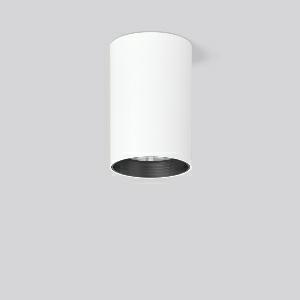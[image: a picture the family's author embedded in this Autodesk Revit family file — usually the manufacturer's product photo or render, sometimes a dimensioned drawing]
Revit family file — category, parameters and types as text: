
# Revit family: heledon_maxi_a_931229_002_76_18f5
name_source: partatom
category: Lighting Fixtures
units: mm (PartAtom-declared; Revit-internal decimal feet)

## family parameters
Cut with Voids When Loaded = No
Host = Face
Light Source = No
Part Type = Normal
Room Calculation Point = No
Round Connector Dimension = Use Diameter
Shared = No

## types (1)
- HELEDON maxi A (1 x LED Modul 930, 3600 lm, 3000)
    Apparent Load = 35 VA
    Approval mark = CE
    CIE Flux Codes = 96 100 100 100 100
    Color Rendering = 90
    Color Temperature = 3000
    Default Elevation = 1800 mm
    Description = Series: HELEDON maxi
Cylindrical surface-mounted downlight. Housing: die-cast aluminium, powder-coated. Internal ceiling frame polycarbonate with bayonet mounting. Black plastic ring and recessed LED to prevent glare from the side. Optical assembly with lens made of plastic (polycarbonate) for the best homogeneous light distribution - can be changed without tools. Best colour rendering index Ra>90. Suitable for Ceiling mounting. Easy installation with a separate ceiling frame with bayonet mounting and plug connection. Driver integrated. Connected via plug-in connector. High quality converter without flickering and stroboscopic effect. The following accessories can be mounted without use of tools: interchangeable lenses, decorative glasses, honeycomb louvre, clear and frosted diffusers, white interchangeable plastic ring. 
Colour: traffic white, matt (RAL 9016)
Diameter: 123 mm
Height: 183 mm
Lamp: LED
Socket: without socket
Colour temperature: 3000K
Colour rendering index (CRI): 92
System power: 35 W
Rated luminous flux: 3600 lm
Luminous efficiency: 103 lm/W
Control gear: Converter, dimmable, DALI
Protection class: I
Type of protection: IP 20
    Height = 183 mm
    Lamp = 1 x LED Modul 930
    Lamp Light Flux = 3600 lm
    Lamp count = 1
    Length = 123 mm
    Lifetime = 50000 h
    Luminous efficacy = 103 lm/W
    Manufacturer = RZB
    ModVariant = No
    Model = 931229.002.76
    Mounting Place = Ceiling
    Mounting Type = Surface mounted
    Number of Poles = 1
    OnlyDefault = Yes
    Power Factor = 1
    Product Name = HELEDON maxi A
    Product group = Surface mounted downlights
    ProductGroupID = 302
    Protection Class = Protection class I
    Protection Degree = IP 20
    RLX_Detail_Level = 1
    RLX_Emergency_Light_Flux = 0 lm
    RLX_Emergency_Type = 0
    RLX_Emergency_Type_DB = No
    RlxData = <blob elided: 98145 chars, md5=e1d3735d>
    Socket = socket
    Standby Power = 0 W
    System Light Flux = 3600 lm
    System Power = 35 W
    Type Comments = Product without accessories
    Type Image = 931193.002.jpg
    URL = http://relux.com
    VarID = ---
    Voltage = 230 V
    Voltage Range = 220-240 V
    Weight = 0.00 kg
    Width = 0 mm  [stored 0 ft]

note: [stored X ft] marks values corroborated as IEEE doubles in the binary element streams (Revit-internal decimal feet)

## geometry (parser evidence)
native form markers: Blend x4, Sweep x10
no freeform markers — native parametric forms only
